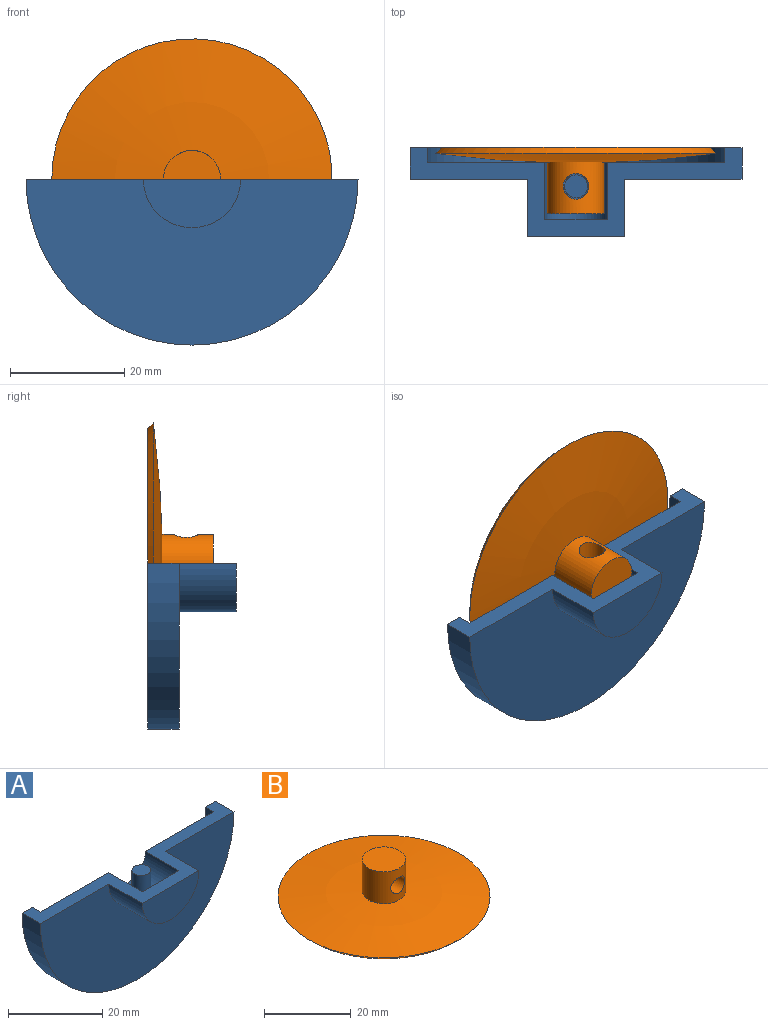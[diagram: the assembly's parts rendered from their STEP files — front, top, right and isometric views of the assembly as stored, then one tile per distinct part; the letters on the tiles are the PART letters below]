
ASSEMBLY  parts=2 mates=1
PART A: 12 faces, bbox 58x15.5x29 mm
  f0: cylinder r=8.5mm len=17mm, axis (0,1,0), area 267mm2, adj f1,f8,f9
  f1: plane 17x8.5mm, normal (0,-1,0), area 113.5mm2, adj f0,f9
  f2: plane 11x5.5mm, normal (0,1,0), area 47.5mm2, adj f3,f9
  f3: cylinder r=5.5mm len=11mm, axis (0,1,0), area 160mm2, adj f2,f4,f9,f11
  f4: plane 52x26mm, normal (0,1,0), area 1014.3mm2, adj f3,f5,f9
  f5: cylinder r=26mm len=52mm, axis (0,1,0), area 204.2mm2, adj f4,f6,f9
  f6: plane 58x29mm, normal (0,1,0), area 259.2mm2, adj f5,f7,f9
  f7: cylinder r=29mm len=58mm, axis (0,1,0), area 501.1mm2, adj f6,f8,f9
  f8: plane 58x29mm, normal (0,-1,0), area 1207.5mm2, adj f0,f7,f9
  f9: plane 58x15.5mm, normal (0,0,1), area 249mm2, adj f0,f1,f2,f3,f4,f5,f6,f7
  f10: plane 4x4mm, normal (0,0,1), area 12.6mm2, adj f11
  f11: cylinder r=2mm len=5.5mm, axis (0,0,1), area 66.8mm2, adj f3,f10
PART B: 6 faces, bbox 49x49x11.5 mm
  f0: revolved ~47x47mm, area 1735.8mm2, adj f4
  f1: plane 10x10mm, normal (0,0,1), area 78.5mm2, adj f2
  f2: cylinder r=5mm len=10mm, axis (0,0,-1), area 250mm2, adj f1,f3,f5
  f3: revolved ~49x49mm, area 1815.2mm2, adj f2,f4
  f4: cone r=24.5mm half-angle=45deg, axis (0,0,1), area 213.3mm2, adj f0,f3
  f5: cylinder r=2.25mm len=10mm, axis (0,-1,0), area 133.9mm2, adj f2
PLACE A t=(-0.1,6.79,0.01)mm fixed
PLACE B rot(axis=(1,0,0),90deg) t=(-0.1,6.79,0.01)mm
MATE slider B.f5 <-> A.f11  axis (0,0,-1) through (-0.1,0.04,0.01)mm
